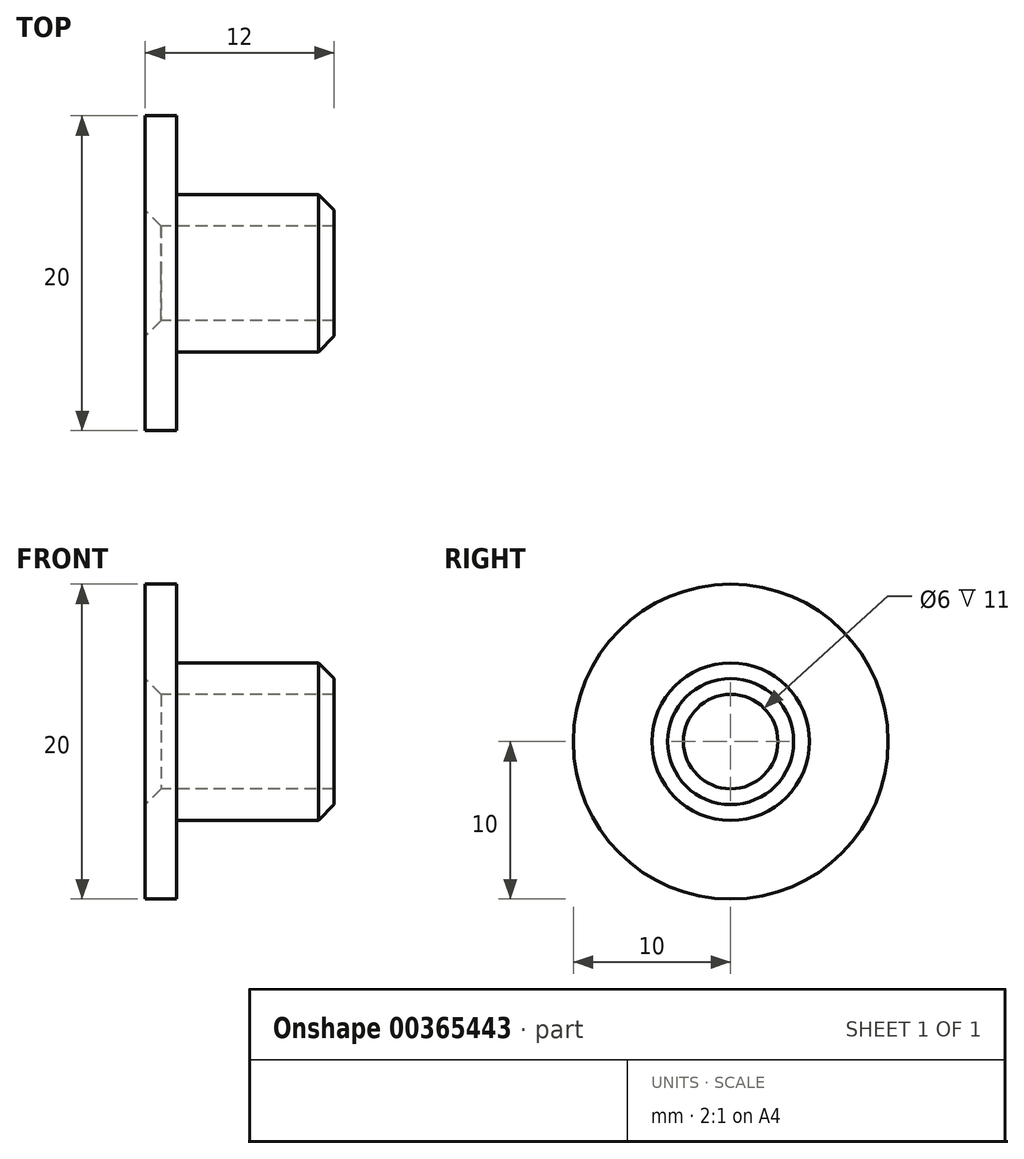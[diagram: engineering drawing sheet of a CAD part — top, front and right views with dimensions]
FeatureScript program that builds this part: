
annotation { "Feature Type Name" : "Feature", "Feature Type Description" : "" }
export const myFeature = defineFeature(function(context is Context, id is Id, definition is map)
    precondition{}
    {
        {
            var Q0;
            Q0=qCreatedBy(makeId("Front.planeOp"),FACE);
            var sketch = newSketch(context, id + "F0", { "sketchPlane" : qUnion([Q0])});
            skLineSegment(sketch, "E0", {"start": v(0, 5) * mm, "end": v(-10, 5) * mm});
            skLineSegment(sketch, "E1", {"start": v(-12, 3) * mm, "end": v(0, 3) * mm});
            skLineSegment(sketch, "E2", {"start": v(0, 3) * mm, "end": v(0, 5) * mm});
            skLineSegment(sketch, "E3", {"start": v(-12, 10) * mm, "end": v(-10, 10) * mm});
            skLineSegment(sketch, "E4", {"start": v(-10, 10) * mm, "end": v(-10, 5) * mm});
            skLineSegment(sketch, "E5", {"start": v(-12, 3) * mm, "end": v(-12, 10) * mm});
            skLineSegment(sketch, "E6", {"start": v(-19.19, 0) * mm, "end": v(5.47, 0) * mm, "construction": true});
            skSolve(sketch);
        }
        {
            var Q0;
            Q0 = qSketchRegion(id + "F0", true);
            var Q1;
            Q1=sQuery(id+"F0.wireOp",EDGE,"E6");
            revolve(context, id + "F1", {"entities" : qUnion([Q0]), "axis" : qUnion([Q1]), "revolveType" : RevolveType.FULL});
        }
        {
            var Q0;
            Q0=makeQuery(id+"F1.opRevolve","SWEPT_EDGE",EDGE,{"disambiguationData":[OSD([sQuery(id+"F0.wireOp",EDGE,"E0"),sQuery(id+"F0.wireOp",EDGE,"E2")])]});
            var Q1;
            Q1=makeQuery(id+"F1.opRevolve","SWEPT_EDGE",EDGE,{"disambiguationData":[OSD([sQuery(id+"F0.wireOp",EDGE,"E1"),sQuery(id+"F0.wireOp",EDGE,"E5")])]});
            chamfer(context, id + "F2", {"entities" : qUnion([Q0, Q1]), "width" : 1 * mm, "tangentPropagation" : true});
        }
    });
